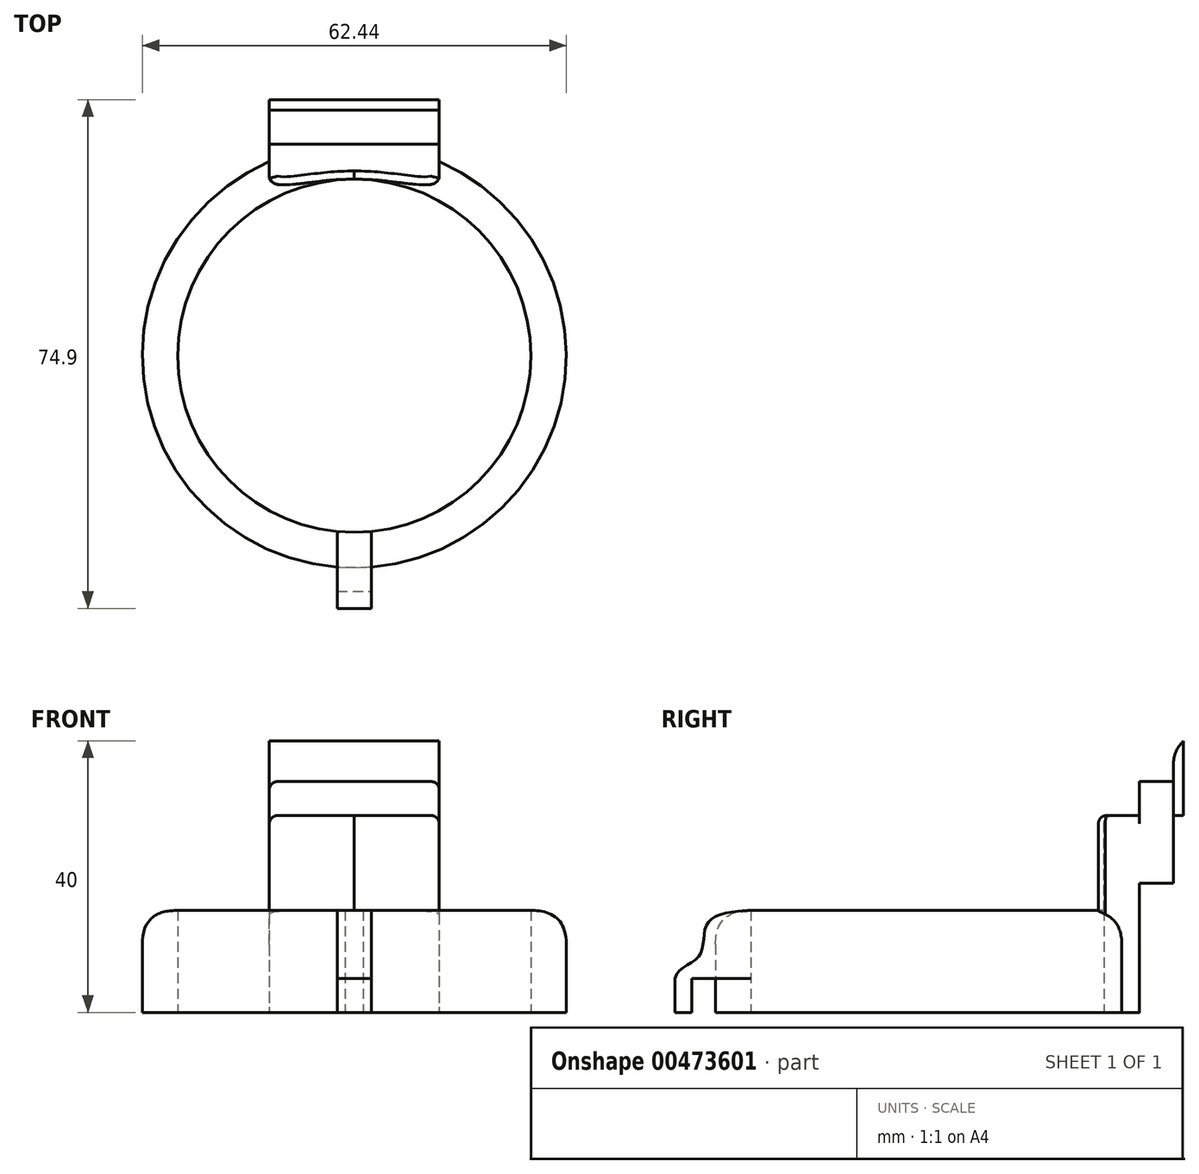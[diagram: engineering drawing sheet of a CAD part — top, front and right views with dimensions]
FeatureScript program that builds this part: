
annotation { "Feature Type Name" : "Feature", "Feature Type Description" : "" }
export const myFeature = defineFeature(function(context is Context, id is Id, definition is map)
    precondition{}
    {
        {
            var Q0;
            Q0=qCreatedBy(makeId("Top.planeOp"),FACE);
            var sketch = newSketch(context, id + "F0", { "sketchPlane" : qUnion([Q0])});
            skCircle(sketch, "E0", {"center": v(0, 0) * mm, "radius": 26 * mm});
            skCircle(sketch, "E1", {"center": v(0, 0) * mm, "radius": 31.22 * mm});
            skPoint(sketch, "E2", {"position": v(0, 31.22) * mm});
            skSolve(sketch);
        }
        {
            var Q0;
            Q0=makeQuery(id+"F0.imprint","IMPRINT",FACE,{"disambiguationData":[TD([[makeQuery(id+"F0.imprint","IMPRINT",EDGE,{"derivedFrom":sQuery(id+"F0.wireOp",EDGE,"E0")}),-1.0]])]});
            extrude(context, id + "F1", {"entities" : qUnion([Q0]), "depth" : 10 * mm, "hasSecondDirection" : true, "secondDirectionOppositeDirection" : true, "secondDirectionDepth" : 5 * mm});
        }
        {
            var Q0;
            Q0=qCreatedBy(makeId("Top.planeOp"),FACE);
            var sketch = newSketch(context, id + "F2", { "sketchPlane" : qUnion([Q0])});
            skLineSegment(sketch, "E3.bottom", {"start": v(-12.5, 31.2) * mm, "end": v(12.5, 31.2) * mm});
            skLineSegment(sketch, "E3.top", {"start": v(-12.5, 26.2) * mm, "end": v(12.5, 26.2) * mm});
            skLineSegment(sketch, "E3.left", {"start": v(-12.5, 31.2) * mm, "end": v(-12.5, 26.2) * mm});
            skLineSegment(sketch, "E3.right", {"start": v(12.5, 31.2) * mm, "end": v(12.5, 26.2) * mm});
            skLineSegment(sketch, "E4", {"start": v(-12.5, 31.2) * mm, "end": v(12.5, 26.2) * mm, "construction": true});
            skLineSegment(sketch, "E5", {"start": v(-12.5, 26.2) * mm, "end": v(12.5, 31.2) * mm, "construction": true});
            skPoint(sketch, "E6", {"position": v(0, 28.7) * mm});
            skSolve(sketch);
        }
        {
            var Q0;
            Q0 = qSketchRegion(id + "F2", true);
            extrude(context, id + "F3", {"entities" : qUnion([Q0]), "operationType" : NewBodyOperationType.ADD, "depth" : 24 * mm, "hasSecondDirection" : true, "secondDirectionOppositeDirection" : true, "secondDirectionDepth" : 5 * mm});
        }
        {
            var Q0;
            Q0=makeQuery(id+"F3.opExtrude","CAP_FACE",FACE,{"disambiguationData":[OSD([sQuery(id+"F2.wireOp",EDGE,"E3.bottom"),sQuery(id+"F2.wireOp",EDGE,"E3.top"),sQuery(id+"F2.wireOp",EDGE,"E3.left"),sQuery(id+"F2.wireOp",EDGE,"E3.right")])],"isStart":false});
            var sketch = newSketch(context, id + "F4", { "sketchPlane" : qUnion([Q0])});
            skLineSegment(sketch, "E7.bottom", {"start": v(-12.5, 31.2) * mm, "end": v(12.5, 31.2) * mm});
            skLineSegment(sketch, "E7.top", {"start": v(-12.5, 36.2) * mm, "end": v(12.5, 36.2) * mm});
            skLineSegment(sketch, "E7.left", {"start": v(-12.5, 31.2) * mm, "end": v(-12.5, 36.2) * mm});
            skLineSegment(sketch, "E7.right", {"start": v(12.5, 31.2) * mm, "end": v(12.5, 36.2) * mm});
            skSolve(sketch);
        }
        {
            var Q0;
            Q0 = qSketchRegion(id + "F4", true);
            extrude(context, id + "F5", {"entities" : qUnion([Q0]), "operationType" : NewBodyOperationType.ADD, "oppositeDirection" : true, "depth" : 10 * mm, "hasSecondDirection" : true, "secondDirectionOppositeDirection" : false, "secondDirectionDepth" : 5 * mm});
        }
        {
            var Q0;
            Q0=makeQuery(id+"F5.opExtrude","CAP_FACE",FACE,{"disambiguationData":[OSD([sQuery(id+"F4.wireOp",EDGE,"E7.bottom"),sQuery(id+"F4.wireOp",EDGE,"E7.top"),sQuery(id+"F4.wireOp",EDGE,"E7.left"),sQuery(id+"F4.wireOp",EDGE,"E7.right")])],"isStart":true});
            var sketch = newSketch(context, id + "F6", { "sketchPlane" : qUnion([Q0])});
            skLineSegment(sketch, "E8.bottom", {"start": v(-12.5, 36.2) * mm, "end": v(12.51, 36.2) * mm});
            skLineSegment(sketch, "E8.top", {"start": v(-12.5, 37.7) * mm, "end": v(12.51, 37.7) * mm});
            skLineSegment(sketch, "E8.left", {"start": v(-12.5, 36.2) * mm, "end": v(-12.5, 37.7) * mm});
            skLineSegment(sketch, "E8.right", {"start": v(12.51, 36.2) * mm, "end": v(12.51, 37.7) * mm});
            skSolve(sketch);
        }
        {
            var Q0;
            Q0=qCreatedBy(makeId("Right.planeOp"),FACE);
            var sketch = newSketch(context, id + "F7", { "sketchPlane" : qUnion([Q0])});
            skFitSpline(sketch, "E9", {"points": [v(-37.2, 0) * mm, v(-33.61, 3.33) * mm, v(-32.43, 8.1) * mm, v(-26.05, 10) * mm], "startDerivative": vector(3.1, 16.24) * mm, "endDerivative": vector(22.01, 0.89) * mm});
            skLineSegment(sketch, "E10", {"start": v(-26.05, 10) * mm, "end": v(-26.05, 0) * mm});
            skLineSegment(sketch, "E11", {"start": v(-26.05, 0) * mm, "end": v(-37.2, 0) * mm});
            skSolve(sketch);
        }
        {
            var Q0;
            Q0=makeQuery(id+"F7.imprint","IMPRINT",FACE,{"disambiguationData":[TD([[makeQuery(id+"F7.imprint","IMPRINT",EDGE,{"derivedFrom":sQuery(id+"F7.wireOp",EDGE,"E9")}),-1.0]])]});
            extrude(context, id + "F8", {"entities" : qUnion([Q0]), "depth" : 2.5 * mm, "hasSecondDirection" : true, "secondDirectionOppositeDirection" : true, "secondDirectionDepth" : 2.5 * mm});
        }
        {
            var Q0;
            Q0=qCreatedBy(makeId("Top.planeOp"),FACE);
            var sketch = newSketch(context, id + "F9", { "sketchPlane" : qUnion([Q0])});
            skLineSegment(sketch, "E12.bottom", {"start": v(-2.5, -37.2) * mm, "end": v(2.5, -37.2) * mm});
            skLineSegment(sketch, "E12.top", {"start": v(-2.5, -34.7) * mm, "end": v(2.5, -34.7) * mm});
            skLineSegment(sketch, "E12.left", {"start": v(-2.5, -37.2) * mm, "end": v(-2.5, -34.7) * mm});
            skLineSegment(sketch, "E12.right", {"start": v(2.5, -37.2) * mm, "end": v(2.5, -34.7) * mm});
            skSolve(sketch);
        }
        {
            var Q0;
            Q0 = qSketchRegion(id + "F9", true);
            extrude(context, id + "F10", {"entities" : qUnion([Q0]), "operationType" : NewBodyOperationType.ADD, "oppositeDirection" : true, "depth" : 5 * mm});
        }
        {
            var Q0;
            {var subQ0=sQuery(id+"F0.wireOp",EDGE,"E1");var subQ1=sQuery(id+"F0.wireOp",EDGE,"E0");Q0=makeQuery(id+"F3.boolean.opBoolean","SPLIT",FACE,{"disambiguationData":[TD([makeQuery(id+"F1.opExtrude","SWEPT_FACE",FACE,{"disambiguationData":[OSD([subQ1])]})])],"derivedFrom":makeQuery(id+"F1.opExtrude","CAP_FACE",FACE,{"disambiguationData":[OSD([subQ1,subQ0])],"isStart":false})});}
            var sketch = newSketch(context, id + "F11", { "sketchPlane" : qUnion([Q0])});
            skFitSpline(sketch, "E13", {"points": [v(-12.5, 26.2) * mm, v(-11.17, 25.22) * mm, v(0, 26) * mm], "startDerivative": vector(1.94, -5.73) * mm, "endDerivative": vector(20.26, -0.24) * mm});
            skLineSegment(sketch, "E14", {"start": v(0, 26) * mm, "end": v(0, 26.2) * mm});
            skLineSegment(sketch, "E15", {"start": v(0, 26.2) * mm, "end": v(-12.5, 26.2) * mm});
            skFitSpline(sketch, "E16.MirrorCS", {"points": [v(12.5, 26.2) * mm, v(11.17, 25.22) * mm, v(0, 26) * mm], "startDerivative": vector(-1.94, -5.73) * mm, "endDerivative": vector(-20.26, -0.24) * mm});
            skLineSegment(sketch, "E17.MirrorCS", {"start": v(0, 26.2) * mm, "end": v(12.5, 26.2) * mm});
            skSolve(sketch);
        }
        {
            var Q0;
            Q0 = qSketchRegion(id + "F11", true);
            extrude(context, id + "F12", {"entities" : qUnion([Q0]), "operationType" : NewBodyOperationType.ADD, "depth" : 14 * mm});
        }
        {
            var Q0;
            {var subQ0=sQuery(id+"F0.wireOp",EDGE,"E1");Q0=makeQuery(id+"F3.boolean.opBoolean","SPLIT",EDGE,{"disambiguationData":[TD([makeQuery(id+"F3.opExtrude","SWEPT_FACE",FACE,{"disambiguationData":[OSD([sQuery(id+"F2.wireOp",EDGE,"E3.left")])]})])],"derivedFrom":makeQuery(id+"F1.opExtrude","CAP_EDGE",EDGE,{"disambiguationData":[OSD([subQ0])],"isStart":false})});}
            fillet(context, id + "F13", {"entities" : qUnion([Q0]), "radius" : 5 * mm, "tangentPropagation" : true, "rho" : 0.5, "crossSection" : FilletCrossSection.CONIC, "allowEdgeOverflow" : false});
        }
        {
            var Q0;
            Q0=makeQuery(id+"F12.opExtrude","CAP_EDGE",EDGE,{"disambiguationData":[OSD([sQuery(id+"F11.wireOp",EDGE,"E13")])],"isStart":false});
            var Q1;
            Q1=makeQuery(id+"F12.opExtrude","CAP_EDGE",EDGE,{"disambiguationData":[OSD([sQuery(id+"F11.wireOp",EDGE,"E16.MirrorCS")])],"isStart":false});
            var Q2;
            Q2=makeQuery(id+"F5.boolean.opBoolean","MERGE",EDGE,{"derivedFrom":[makeQuery(id+"F3.opExtrude","CAP_EDGE",EDGE,{"disambiguationData":[OSD([sQuery(id+"F2.wireOp",EDGE,"E3.left")])],"isStart":false}),makeQuery(id+"F5.opExtrude","CAP_EDGE",EDGE,{"disambiguationData":[OSD([sQuery(id+"F4.wireOp",EDGE,"E7.left")])],"isStart":true})]});
            var Q3;
            Q3=makeQuery(id+"F5.boolean.opBoolean","MERGE",EDGE,{"derivedFrom":[makeQuery(id+"F3.opExtrude","CAP_EDGE",EDGE,{"disambiguationData":[OSD([sQuery(id+"F2.wireOp",EDGE,"E3.right")])],"isStart":false}),makeQuery(id+"F5.opExtrude","CAP_EDGE",EDGE,{"disambiguationData":[OSD([sQuery(id+"F4.wireOp",EDGE,"E7.right")])],"isStart":true})]});
            fillet(context, id + "F14", {"entities" : qUnion([Q0, Q1, Q2, Q3]), "radius" : 1.2 * mm, "tangentPropagation" : true, "allowEdgeOverflow" : false});
        }
        {
            var Q0;
            Q0=makeQuery(id+"F6.imprint","IMPRINT",FACE,{"disambiguationData":[TD([[makeQuery(id+"F6.imprint","IMPRINT",EDGE,{"derivedFrom":sQuery(id+"F6.wireOp",EDGE,"E8.top")}),-1.0]])]});
            extrude(context, id + "F15", {"entities" : qUnion([Q0]), "operationType" : NewBodyOperationType.ADD, "depth" : 6 * mm, "hasSecondDirection" : true, "secondDirectionOppositeDirection" : true, "secondDirectionDepth" : 5 * mm});
        }
        {
            var Q0;
            Q0=makeQuery(id+"F15.opExtrude","CAP_EDGE",EDGE,{"disambiguationData":[OSD([sQuery(id+"F6.wireOp",EDGE,"E8.bottom")])],"isStart":false});
            fillet(context, id + "F16", {"entities" : qUnion([Q0]), "radius" : 5 * mm, "tangentPropagation" : true, "allowEdgeOverflow" : false});
        }
    });
